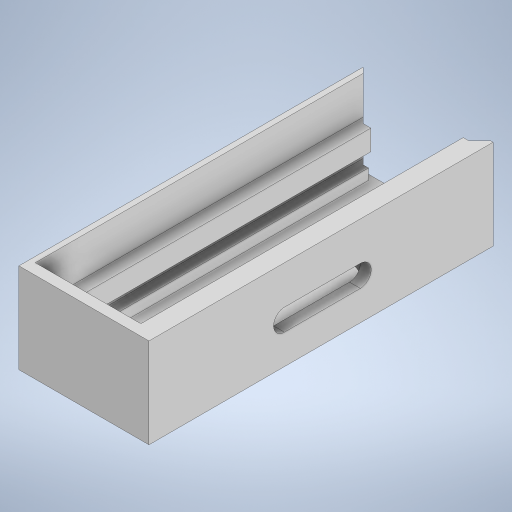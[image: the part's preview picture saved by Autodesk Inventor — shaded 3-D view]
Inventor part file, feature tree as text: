
AUTODESK INVENTOR PART (.ipt)
format: ipt  version: 2023 (Build 270158000, 158)  size: 425,984 bytes
history: native  units: mm
features: sketch x11, extrude x10, projected_geometry x8, plane x3, chamfer x3, fillet x1
ambient origin geometry x8: Origin, YZ Plane, XZ Plane, XY Plane, X Axis, Y Axis, Z Axis, Center Point
bodies: Solid1 (feature_tree)
feature tree (36):
  extrude  "Extrusion1"  Depth=24.0mm
  extrude  "Extrusion2"  Depth=3.0mm
  extrude  "Extrusion3"  Depth=21.0mm
  fillet  "Fillet1"  Radius=1.0mm
  extrude  "Extrusion4"  Depth=14.6mm
  extrude  "Extrusion5"  TaperAngle=0.0deg  [1 undecoded]
  extrude  "Extrusion6"  TaperAngle=30.0deg  [1 undecoded]
  plane  "Work Plane1"
  extrude  "Extrusion7"  Depth=8.5mm
  extrude  "Extrusion8"  Depth=27.3mm
  chamfer  "Chamfer1"  Distance=16.2mm
  chamfer  "Chamfer2"  Distance=1.0mm
  chamfer  "Chamfer3"  Distance=5.0mm
  plane  "Work Plane3"
  sketch  "Sketch12"  dims[d22=0.4mm]
  extrude  "Extrusion9"  Depth=4.0mm
  extrude  "Extrusion10"  Depth=1.0mm
  sketch  "Sketch1"  dims[d0=62.5mm d1=24.0mm]
  sketch  "Sketch2"  dims[d2=16.6mm d3=0.0mm d4=3.0mm]
  sketch  "Sketch4"  dims[d5=1.6mm d6=21.0mm d7=1.0mm]
  sketch  "Sketch5"  dims[d8=19.5mm d10=14.6mm]
  sketch  "Sketch6"  dims[d11=5.0mm d13=0.0mm d14=0.0mm]
  projected_geometry  "Projected Loop1"
  projected_geometry  "Projected Loop2"
  sketch  "Sketch7"  dims[d16=30.0deg d17=30.0deg]
  sketch  "Sketch9"  dims[d18=1.4mm d19=8.5mm]
  projected_geometry  "Projected Loop3"
  projected_geometry  "Projected Loop4"
  sketch  "Sketch10"  dims[d20=1.5mm d21=27.3mm]
  plane  "Work Plane2"
  sketch  "Sketch13"  dims[d23=31.3mm d24=16.2mm d25=0.0mm]
  projected_geometry  "Projected Loop5"
  projected_geometry  "Projected Loop6"
  projected_geometry  "Projected Loop7"
  sketch  "Sketch14"  dims[d26=4.0mm d27=1.0mm d28=0.0mm d29=5.0mm d30=0.0mm d31=4.0mm d32=7.5mm d33=31.0mm d34=14.0mm d35=5.5mm d36=0.0mm d37=-2.0mm d38=20.0mm d40=10.0mm d41=0.0mm d42=2.0mm d43=1.0mm d44=2.0mm d45=10.0mm d46=0.0mm d47=2.5mm d48=2.0mm d49=45.0deg d50=3.0mm d51=2.0mm d52=45.0deg d53=1.0mm d54=2.0mm d55=45.0deg d56=-2.0mm d57=5.0mm d58=0.0mm d59=1.0mm d60=0.0mm]
  projected_geometry  "Projected Loop8"
note: 2 required parameter values undecoded (feature->parameter linkage not recoverable at this tier; creation-order binding heuristic only, values carry confidence <= 0.55)
